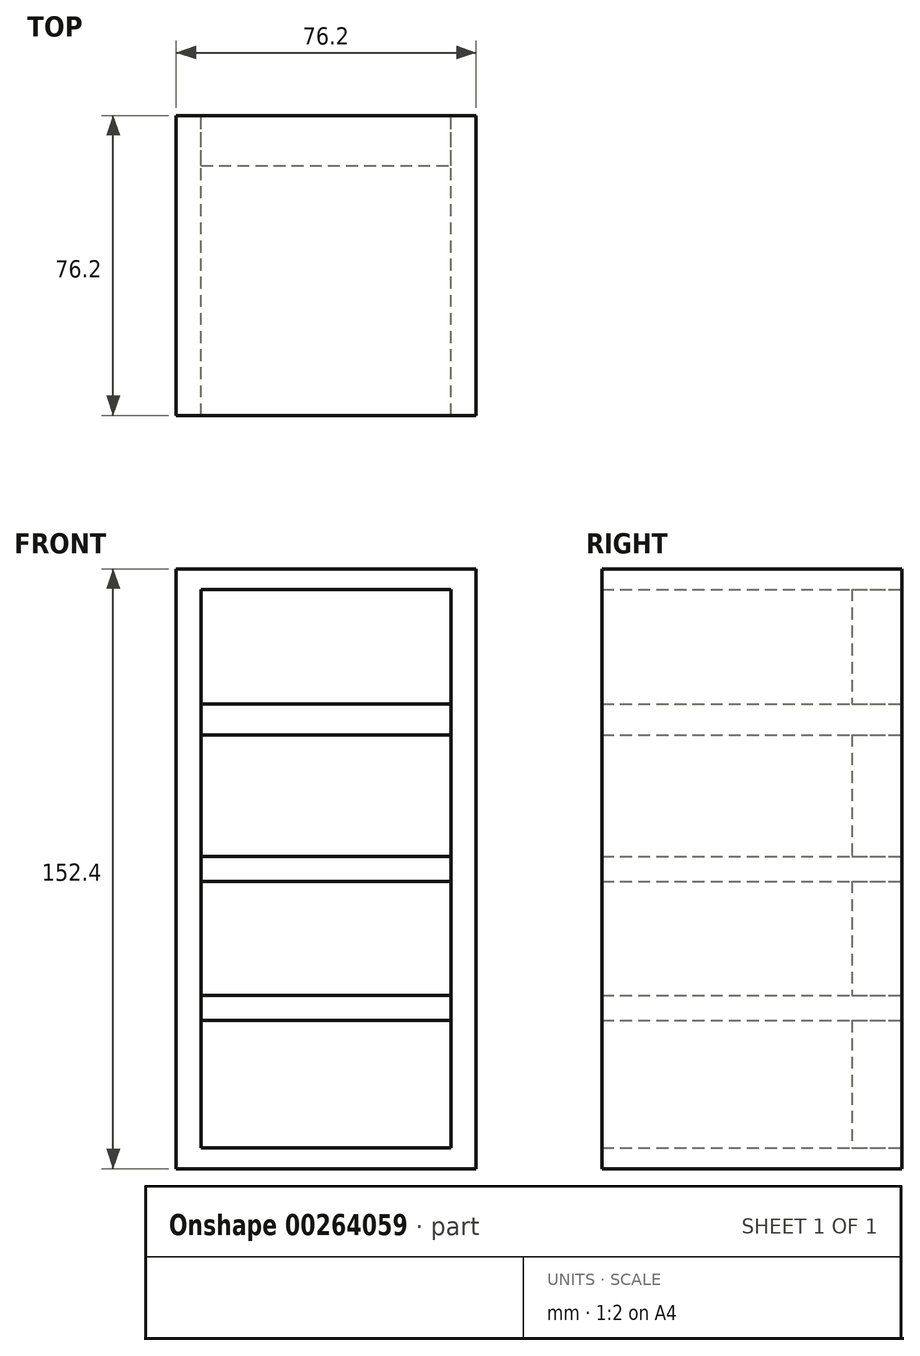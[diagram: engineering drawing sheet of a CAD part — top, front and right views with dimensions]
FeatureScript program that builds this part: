
annotation { "Feature Type Name" : "Feature", "Feature Type Description" : "" }
export const myFeature = defineFeature(function(context is Context, id is Id, definition is map)
    precondition{}
    {
        {
            var Q0;
            Q0=qCreatedBy(makeId("Front.planeOp"),FACE);
            var sketch = newSketch(context, id + "F0", { "sketchPlane" : qUnion([Q0])});
            skLineSegment(sketch, "E0.bottom", {"start": v(-38.1, 76.2) * mm, "end": v(38.1, 76.2) * mm});
            skLineSegment(sketch, "E0.top", {"start": v(-38.1, -76.2) * mm, "end": v(38.1, -76.2) * mm});
            skLineSegment(sketch, "E0.left", {"start": v(-38.1, 76.2) * mm, "end": v(-38.1, -76.2) * mm});
            skLineSegment(sketch, "E0.right", {"start": v(38.1, 76.2) * mm, "end": v(38.1, -76.2) * mm});
            skPoint(sketch, "E0.middle", {"position": v(0, 0) * mm});
            skLineSegment(sketch, "E1.bottom", {"start": v(31.75, 70.98) * mm, "end": v(-31.75, 70.98) * mm});
            skLineSegment(sketch, "E1.top", {"start": v(31.75, -70.98) * mm, "end": v(-31.75, -70.98) * mm});
            skLineSegment(sketch, "E1.left", {"start": v(31.75, 70.98) * mm, "end": v(31.75, -70.98) * mm});
            skLineSegment(sketch, "E1.right", {"start": v(-31.75, 70.98) * mm, "end": v(-31.75, -70.98) * mm});
            skLineSegment(sketch, "E2.bottom", {"start": v(31.75, 3.18) * mm, "end": v(-31.75, 3.18) * mm});
            skLineSegment(sketch, "E2.top", {"start": v(31.75, -3.18) * mm, "end": v(-31.75, -3.18) * mm});
            skLineSegment(sketch, "E2.left", {"start": v(31.75, 3.18) * mm, "end": v(31.75, -3.18) * mm});
            skLineSegment(sketch, "E2.right", {"start": v(-31.75, 3.18) * mm, "end": v(-31.75, -3.18) * mm});
            skLineSegment(sketch, "E3.bottom", {"start": v(-31.75, 41.86) * mm, "end": v(31.75, 41.86) * mm});
            skLineSegment(sketch, "E3.top", {"start": v(-31.75, 34.03) * mm, "end": v(31.75, 34.03) * mm});
            skLineSegment(sketch, "E3.left", {"start": v(-31.75, 41.86) * mm, "end": v(-31.75, 34.03) * mm});
            skLineSegment(sketch, "E3.right", {"start": v(31.75, 41.86) * mm, "end": v(31.75, 34.03) * mm});
            skLineSegment(sketch, "E4.bottom", {"start": v(-31.75, -32.21) * mm, "end": v(31.75, -32.21) * mm});
            skLineSegment(sketch, "E4.top", {"start": v(-31.75, -38.56) * mm, "end": v(31.75, -38.56) * mm});
            skLineSegment(sketch, "E4.left", {"start": v(-31.75, -32.21) * mm, "end": v(-31.75, -38.56) * mm});
            skLineSegment(sketch, "E4.right", {"start": v(31.75, -32.21) * mm, "end": v(31.75, -38.56) * mm});
            skSolve(sketch);
        }
        {
            var Q0;
            Q0=makeQuery(id+"F0.imprint","IMPRINT",FACE,{"disambiguationData":[TD([[makeQuery(id+"F0.imprint","IMPRINT",EDGE,{"derivedFrom":sQuery(id+"F0.wireOp",EDGE,"E0.bottom")}),-1.0]])]});
            extrude(context, id + "F1", {"entities" : qUnion([Q0]), "depth" : 76.2 * mm});
        }
        {
            var Q0;
            Q0=makeQuery(id+"F0.imprint","IMPRINT",FACE,{"disambiguationData":[TD([[makeQuery(id+"F0.imprint","IMPRINT",EDGE,{"derivedFrom":sQuery(id+"F0.wireOp",EDGE,"E1.bottom")}),1.0]])]});
            extrude(context, id + "F2", {"entities" : qUnion([Q0]), "depth" : 12.7 * mm});
        }
        {
            var Q0;
            Q0=makeQuery(id+"F0.imprint","IMPRINT",FACE,{"disambiguationData":[TD([[makeQuery(id+"F0.imprint","IMPRINT",EDGE,{"derivedFrom":sQuery(id+"F0.wireOp",EDGE,"E2.bottom")}),1.0]])]});
            extrude(context, id + "F3", {"entities" : qUnion([Q0]), "depth" : 76.2 * mm});
        }
        {
            var Q0;
            {var subQ0=sQuery(id+"F0.wireOp",EDGE,"E1.top");Q0=makeQuery(id+"F0.imprint","IMPRINT",FACE,{"disambiguationData":[TD([[makeQuery(id+"F0.imprint","IMPRINT",EDGE,{"derivedFrom":subQ0}),-1.0]])]});}
            extrude(context, id + "F4", {"entities" : qUnion([Q0]), "depth" : 12.7 * mm});
        }
        {
            var Q0;
            Q0=makeQuery(id+"F0.imprint","IMPRINT",FACE,{"disambiguationData":[TD([[makeQuery(id+"F0.imprint","IMPRINT",EDGE,{"derivedFrom":sQuery(id+"F0.wireOp",EDGE,"E4.bottom")}),-1.0]])]});
            var Q1;
            Q1=makeQuery(id+"F0.imprint","IMPRINT",FACE,{"disambiguationData":[TD([[makeQuery(id+"F0.imprint","IMPRINT",EDGE,{"derivedFrom":sQuery(id+"F0.wireOp",EDGE,"E3.bottom")}),-1.0]])]});
            extrude(context, id + "F5", {"entities" : qUnion([Q0, Q1]), "depth" : 76.2 * mm});
        }
        {
            var Q0;
            {var subQ0=sQuery(id+"F0.wireOp",EDGE,"E2.bottom");Q0=makeQuery(id+"F0.imprint","IMPRINT",FACE,{"disambiguationData":[TD([[makeQuery(id+"F0.imprint","IMPRINT",EDGE,{"derivedFrom":subQ0}),-1.0]])]});}
            var Q1;
            {var subQ0=sQuery(id+"F0.wireOp",EDGE,"E1.top");Q1=makeQuery(id+"F0.imprint","IMPRINT",FACE,{"disambiguationData":[TD([[makeQuery(id+"F0.imprint","IMPRINT",EDGE,{"derivedFrom":subQ0}),-1.0]])]});}
            extrude(context, id + "F6", {"entities" : qUnion([Q0, Q1]), "depth" : 12.7 * mm});
        }
        {
            var Q0;
            {var subQ0=sQuery(id+"F0.wireOp",EDGE,"E2.top");Q0=makeQuery(id+"F0.imprint","IMPRINT",FACE,{"disambiguationData":[TD([[makeQuery(id+"F0.imprint","IMPRINT",EDGE,{"derivedFrom":subQ0}),1.0]])]});}
            extrude(context, id + "F7", {"entities" : qUnion([Q0]), "depth" : 12.7 * mm});
        }
    });
